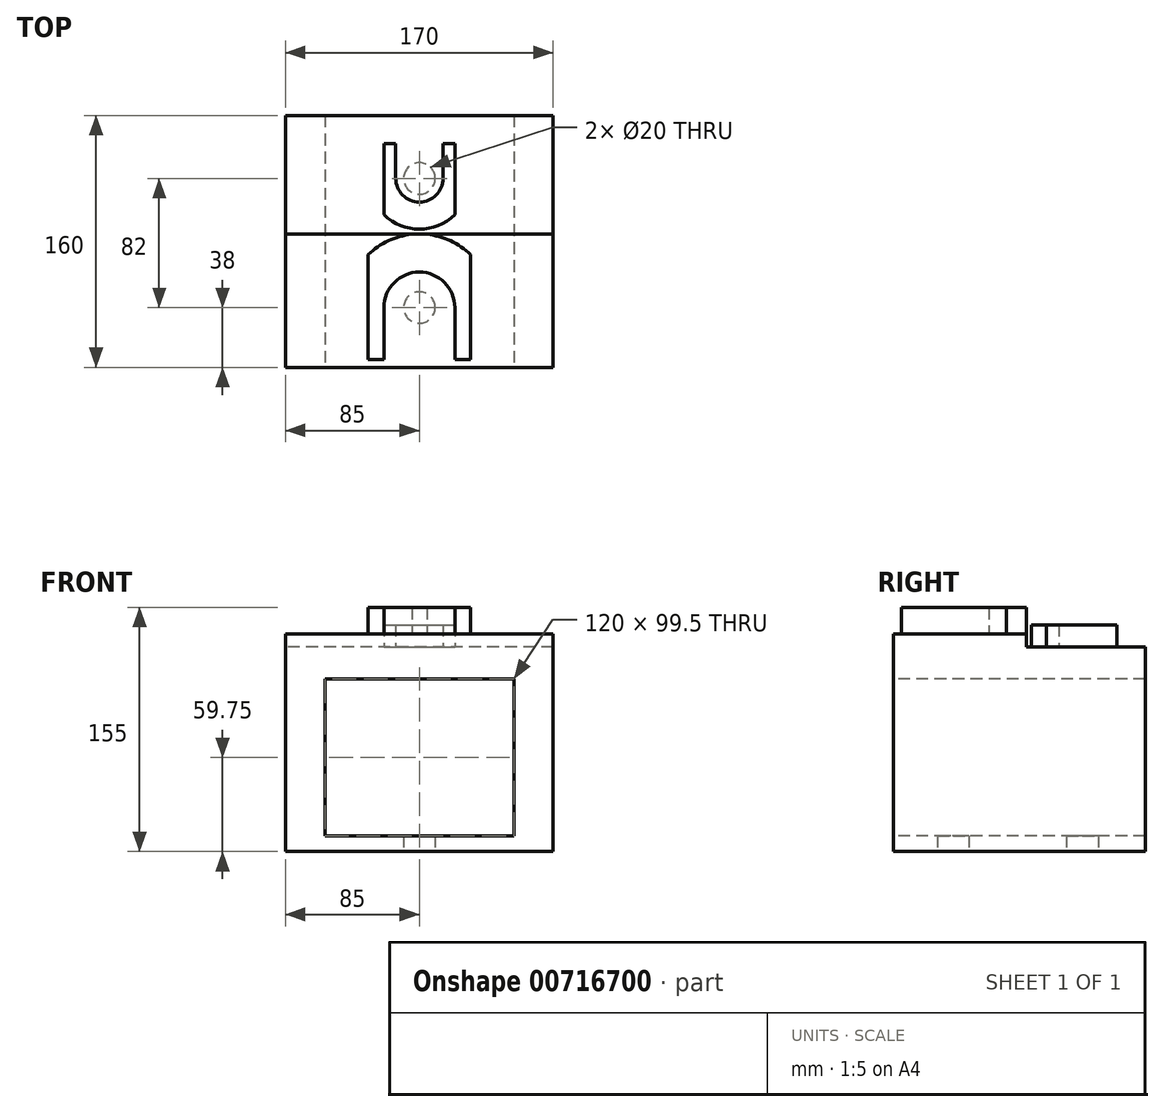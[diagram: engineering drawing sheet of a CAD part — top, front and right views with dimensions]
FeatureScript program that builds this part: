
annotation { "Feature Type Name" : "Feature", "Feature Type Description" : "" }
export const myFeature = defineFeature(function(context is Context, id is Id, definition is map)
    precondition{}
    {
        {
            var Q0;
            Q0=qCreatedBy(makeId("Front.planeOp"),FACE);
            var sketch = newSketch(context, id + "F0", { "sketchPlane" : qUnion([Q0])});
            skLineSegment(sketch, "E0.bottom", {"start": v(-85, 69) * mm, "end": v(85, 69) * mm});
            skLineSegment(sketch, "E0.top", {"start": v(-85, -69) * mm, "end": v(85, -69) * mm});
            skLineSegment(sketch, "E0.left", {"start": v(-85, 69) * mm, "end": v(-85, -69) * mm});
            skLineSegment(sketch, "E0.right", {"start": v(85, 69) * mm, "end": v(85, -69) * mm});
            skLineSegment(sketch, "E1", {"start": v(-85, 0) * mm, "end": v(85, 0) * mm, "construction": true});
            skLineSegment(sketch, "E2", {"start": v(0, 69) * mm, "end": v(0, -69) * mm, "construction": true});
            skPoint(sketch, "E2.endSnap0", {"position": v(0, -69) * mm});
            skLineSegment(sketch, "E3.bottom", {"start": v(-60, 40.5) * mm, "end": v(60, 40.5) * mm});
            skLineSegment(sketch, "E3.top", {"start": v(-60, -59) * mm, "end": v(60, -59) * mm});
            skLineSegment(sketch, "E3.left", {"start": v(-60, 40.5) * mm, "end": v(-60, -59) * mm});
            skLineSegment(sketch, "E3.right", {"start": v(60, 40.5) * mm, "end": v(60, -59) * mm});
            skSolve(sketch);
        }
        {
            var Q0;
            Q0=makeQuery(id+"F0.imprint","IMPRINT",FACE,{"disambiguationData":[TD([[makeQuery(id+"F0.imprint","IMPRINT",EDGE,{"derivedFrom":sQuery(id+"F0.wireOp",EDGE,"E0.bottom")}),-1.0]])]});
            extrude(context, id + "F1", {"entities" : qUnion([Q0]), "oppositeDirection" : true, "depth" : 160 * mm, "offsetDistance" : 25 * mm});
        }
        {
            var Q0;
            Q0=makeQuery(id+"F1.opExtrude","CAP_FACE",FACE,{"disambiguationData":[OSD([sQuery(id+"F0.wireOp",EDGE,"E0.bottom"),sQuery(id+"F0.wireOp",EDGE,"E0.top"),sQuery(id+"F0.wireOp",EDGE,"E0.left"),sQuery(id+"F0.wireOp",EDGE,"E0.right"),sQuery(id+"F0.wireOp",EDGE,"E3.bottom"),sQuery(id+"F0.wireOp",EDGE,"E3.top"),sQuery(id+"F0.wireOp",EDGE,"E3.left"),sQuery(id+"F0.wireOp",EDGE,"E3.right")])],"isStart":false});
            var sketch = newSketch(context, id + "F2", { "sketchPlane" : qUnion([Q0])});
            skLineSegment(sketch, "E4.0", {"start": v(-85, 69) * mm, "end": v(-85, -69) * mm});
            skLineSegment(sketch, "E5.0", {"start": v(85, 69) * mm, "end": v(-85, 69) * mm});
            skLineSegment(sketch, "E6.0", {"start": v(85, 69) * mm, "end": v(85, -69) * mm});
            skLineSegment(sketch, "E7", {"start": v(-85, 61) * mm, "end": v(85, 61) * mm});
            skSolve(sketch);
        }
        {
            var Q0;
            {var subQ0=sQuery(id+"F2.wireOp",EDGE,"E5.0");Q0=makeQuery(id+"F2.imprint","IMPRINT",FACE,{"disambiguationData":[TD([[makeQuery(id+"F2.imprint","IMPRINT",EDGE,{"derivedFrom":subQ0}),1.0]])]});}
            extrude(context, id + "F3", {"entities" : qUnion([Q0]), "operationType" : NewBodyOperationType.REMOVE, "oppositeDirection" : true, "depth" : 75.5 * mm, "offsetDistance" : 25 * mm});
        }
        {
            var Q0;
            Q0=makeQuery(id+"F1.opExtrude","SWEPT_FACE",FACE,{"disambiguationData":[OSD([sQuery(id+"F0.wireOp",EDGE,"E0.top")])]});
            var sketch = newSketch(context, id + "F4", { "sketchPlane" : qUnion([Q0])});
            skLineSegment(sketch, "E8", {"start": v(0, 0) * mm, "end": v(0, -160) * mm, "construction": true});
            skCircle(sketch, "E9", {"center": v(0, -38) * mm, "radius": 10 * mm});
            skCircle(sketch, "E10", {"center": v(0, -120) * mm, "radius": 10 * mm});
            skSolve(sketch);
        }
        {
            var Q0;
            Q0=makeQuery(id+"F4.imprint","IMPRINT",FACE,{"disambiguationData":[TD([[makeQuery(id+"F4.imprint","IMPRINT",EDGE,{"derivedFrom":sQuery(id+"F4.wireOp",EDGE,"E10")}),1.0]])]});
            var Q1;
            Q1=makeQuery(id+"F4.imprint","IMPRINT",FACE,{"disambiguationData":[TD([[makeQuery(id+"F4.imprint","IMPRINT",EDGE,{"derivedFrom":sQuery(id+"F4.wireOp",EDGE,"E9")}),1.0]])]});
            extrude(context, id + "F5", {"entities" : qUnion([Q0, Q1]), "operationType" : NewBodyOperationType.REMOVE, "oppositeDirection" : true, "depth" : 25 * mm, "offsetDistance" : 25 * mm});
        }
        {
            var Q0;
            Q0=qCreatedBy(makeId("Right.planeOp"),FACE);
            var sketch = newSketch(context, id + "F6", { "sketchPlane" : qUnion([Q0])});
            skLineSegment(sketch, "E11.0", {"start": v(130, -59) * mm, "end": v(110, -59) * mm});
            skLineSegment(sketch, "E12", {"start": v(120, -59) * mm, "end": v(120, 91) * mm, "construction": true});
            skLineSegment(sketch, "E13.0", {"start": v(48, -59) * mm, "end": v(28, -59) * mm});
            skLineSegment(sketch, "E14", {"start": v(38, -59) * mm, "end": v(38, 91) * mm, "construction": true});
            skSolve(sketch);
        }
        {
            var Q0;
            Q0=makeQuery(id+"F3.boolean.opBoolean","COPY",FACE,{"derivedFrom":makeQuery(id+"F3.opExtrude","SWEPT_FACE",FACE,{"disambiguationData":[OSD([sQuery(id+"F2.wireOp",EDGE,"E7")])]})});
            var sketch = newSketch(context, id + "F7", { "sketchPlane" : qUnion([Q0])});
            skLineSegment(sketch, "E15", {"start": v(15, 137.66) * mm, "end": v(15, 120) * mm});
            skLineSegment(sketch, "E16", {"start": v(-15, 120) * mm, "end": v(-15, 142) * mm});
            skArc(sketch, "E17", {"start": v(-15, 120) * mm, "mid": v(0, 105) * mm, "end": v(15, 120) * mm});
            skLineSegment(sketch, "E18", {"start": v(15, 120) * mm, "end": v(-15, 120) * mm, "construction": true});
            skLineSegment(sketch, "E19", {"start": v(-22.5, 120) * mm, "end": v(-22.5, 97) * mm});
            skLineSegment(sketch, "E20", {"start": v(-15, 120) * mm, "end": v(-22.5, 120) * mm, "construction": true});
            skLineSegment(sketch, "E21", {"start": v(22.5, 120) * mm, "end": v(22.5, 97) * mm});
            skLineSegment(sketch, "E22", {"start": v(15, 120) * mm, "end": v(22.5, 120) * mm, "construction": true});
            skArc(sketch, "E23", {"start": v(-22.5, 97) * mm, "mid": v(0, 87.75) * mm, "end": v(22.5, 97) * mm});
            skLineSegment(sketch, "E24", {"start": v(-22.5, 120) * mm, "end": v(-22.5, 142) * mm});
            skLineSegment(sketch, "E25", {"start": v(-22.5, 142) * mm, "end": v(-15, 142) * mm});
            skLineSegment(sketch, "E26", {"start": v(15, 137.66) * mm, "end": v(15, 142) * mm});
            skLineSegment(sketch, "E27", {"start": v(15, 142) * mm, "end": v(22.5, 142) * mm});
            skLineSegment(sketch, "E28", {"start": v(22.5, 142) * mm, "end": v(22.5, 120) * mm});
            skSolve(sketch);
        }
        {
            var Q0;
            Q0=makeQuery(id+"F7.imprint","IMPRINT",FACE,{"disambiguationData":[TD([[makeQuery(id+"F7.imprint","IMPRINT",EDGE,{"derivedFrom":sQuery(id+"F7.wireOp",EDGE,"E15")}),1.0]])]});
            extrude(context, id + "F8", {"entities" : qUnion([Q0]), "depth" : 14 * mm, "offsetDistance" : 25 * mm});
        }
        {
            var Q0;
            Q0=makeQuery(id+"F1.opExtrude","SWEPT_FACE",FACE,{"disambiguationData":[OSD([sQuery(id+"F0.wireOp",EDGE,"E0.bottom")])]});
            var sketch = newSketch(context, id + "F9", { "sketchPlane" : qUnion([Q0])});
            skLineSegment(sketch, "E29.0", {"start": v(0, 48) * mm, "end": v(0, 28) * mm});
            skCircle(sketch, "E30", {"center": v(0, 38) * mm, "radius": 22.5 * mm});
            skLineSegment(sketch, "E31", {"start": v(-32.5, 71.6) * mm, "end": v(-32.5, 5) * mm});
            skLineSegment(sketch, "E32", {"start": v(32.5, 71.6) * mm, "end": v(32.5, 5) * mm});
            skCircle(sketch, "E33", {"center": v(0, 38) * mm, "radius": 46.75 * mm, "construction": true});
            skArc(sketch, "E34", {"start": v(32.5, 71.6) * mm, "mid": v(0, 84.75) * mm, "end": v(-32.5, 71.6) * mm});
            skLineSegment(sketch, "E35", {"start": v(-32.5, 5) * mm, "end": v(32.5, 5) * mm});
            skLineSegment(sketch, "E36", {"start": v(-22.5, 38) * mm, "end": v(-22.5, 5) * mm});
            skLineSegment(sketch, "E37", {"start": v(22.5, 38) * mm, "end": v(22.5, 5) * mm});
            skSolve(sketch);
        }
        {
            var Q0;
            {var subQ4=sQuery(id+"F9.wireOp",EDGE,"E31");Q0=makeQuery(id+"F9.imprint","IMPRINT",FACE,{"disambiguationData":[TD([[makeQuery(id+"F9.imprint","IMPRINT",EDGE,{"derivedFrom":subQ4}),1.0]])]});}
            extrude(context, id + "F10", {"entities" : qUnion([Q0]), "depth" : 17 * mm, "offsetDistance" : 25 * mm});
        }
    });
